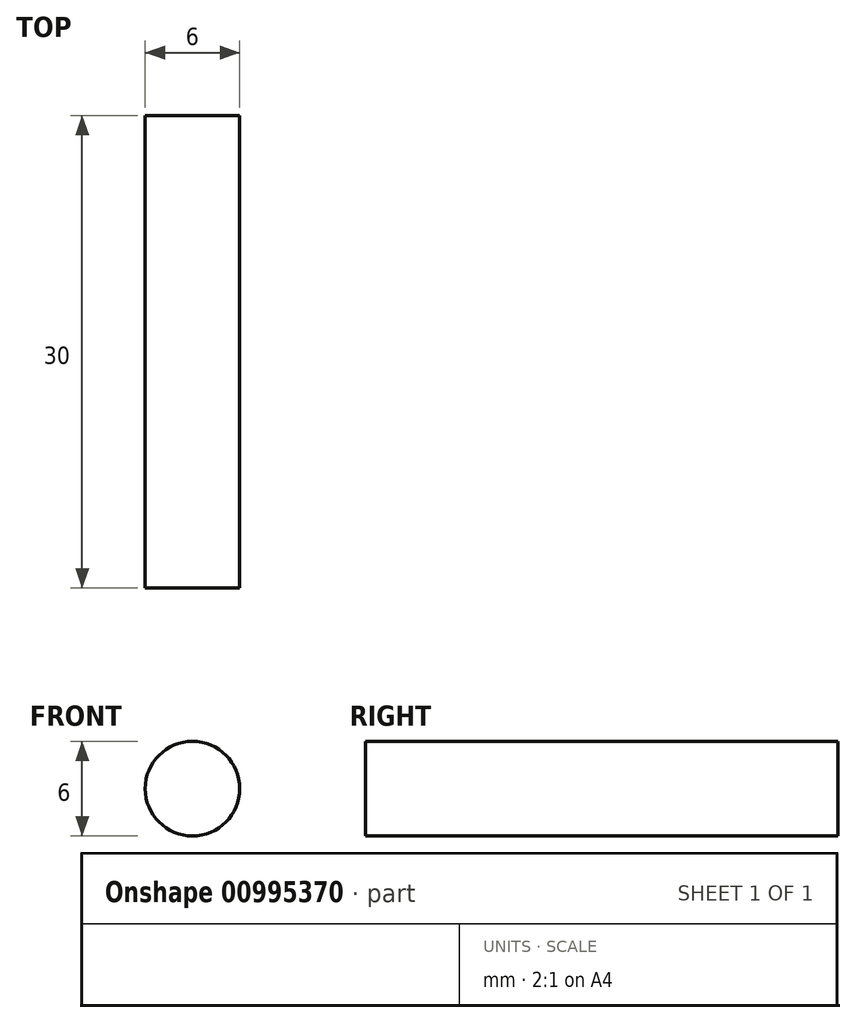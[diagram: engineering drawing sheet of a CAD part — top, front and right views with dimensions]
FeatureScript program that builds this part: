
annotation { "Feature Type Name" : "Feature", "Feature Type Description" : "" }
export const myFeature = defineFeature(function(context is Context, id is Id, definition is map)
    precondition{}
    {
        {
            var Q0;
            Q0=qCreatedBy(makeId("Front.planeOp"),FACE);
            var sketch = newSketch(context, id + "F0", { "sketchPlane" : qUnion([Q0])});
            skCircle(sketch, "E0", {"center": v(0, 0) * mm, "radius": 3 * mm});
            skSolve(sketch);
        }
        {
            var Q0;
            Q0=sQuery(id+"F0.wireOp",EDGE,"E0");
            extrude(context, id + "F1", {"bodyType" : ToolBodyType.SURFACE, "operationType" : NewBodyOperationType.ADD, "surfaceEntities" : qUnion([Q0]), "depth" : 30 * mm, "offsetDistance" : 25 * mm});
        }
    });
